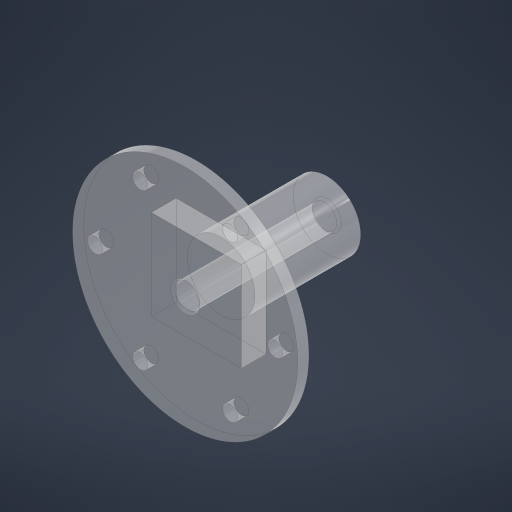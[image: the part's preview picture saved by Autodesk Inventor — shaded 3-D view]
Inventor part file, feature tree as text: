
AUTODESK INVENTOR PART (.ipt)
format: ipt  version: 2024.1 (Build 281209000, 209)  size: 271,872 bytes
history: native  units: in
note: dims shown in document units (in); Inventor stores cm internally (conversion verified against a paired STEP export)
features: extrude x6, other x5, sketch x4, reference x3, plane x1, chamfer x1
ambient origin geometry x8: Origin, YZ Plane, XZ Plane, XY Plane, X Axis, Y Axis, Z Axis, Center Point
bodies: Solid1 (feature_tree)
feature tree (20):
  extrude  "Extrusion1"  Depth=0.003in
  plane  "Work Plane1"
  sketch  "Sketch2"  dims[d2=0.5906in d3=5.0787in d4=0.0in d5=0.0in d6=5.4134in]
  extrude  "Extrusion2"  Depth=5.4134in
  extrude  "Extrusion3"  Depth=1.0in
  extrude  "Extrusion4"  Depth=0.125in
  extrude  "Extrusion5"  Depth=0.125in
  extrude  "Extrusion6"  Depth=1.0in
  chamfer  "Chamfer2"  Distance=2.3622in Angle=360.0deg
  sketch  "Sketch1"  dims[d0=0.002in d1=0.003in]
  reference  "Reference1"
  reference  "Reference2"
  sketch  "Sketch3"  dims[d7=21.6535in d8=1.0in]
  sketch  "Sketch4"  dims[d9=2.5in d10=24.0in d11=0.1654in d12=1.0in d13=2.3622in d15=360.0deg d17=1.0in d18=1.0in d19=0.75in d20=1.5748in d21=0.0in d22=0.4in d23=0.0in d24=0.125in d25=0.0in d29=0.005in d30=0.0in d31=0.0in d32=0.01in d33=1.5748in d34=0.0in d35=0.025in d36=0.125in d37=45.0deg]
  reference  "Reference3"
  other  "Assembly1"
  other  "BallBearing_8x22x7mm:1"
  other  "AcrylicRod:1"
  other  "<userpath>\Documents\School\FallCAD\Trebuchet\Trebuchet.iam"
  other  "Trebuchet.iam"
